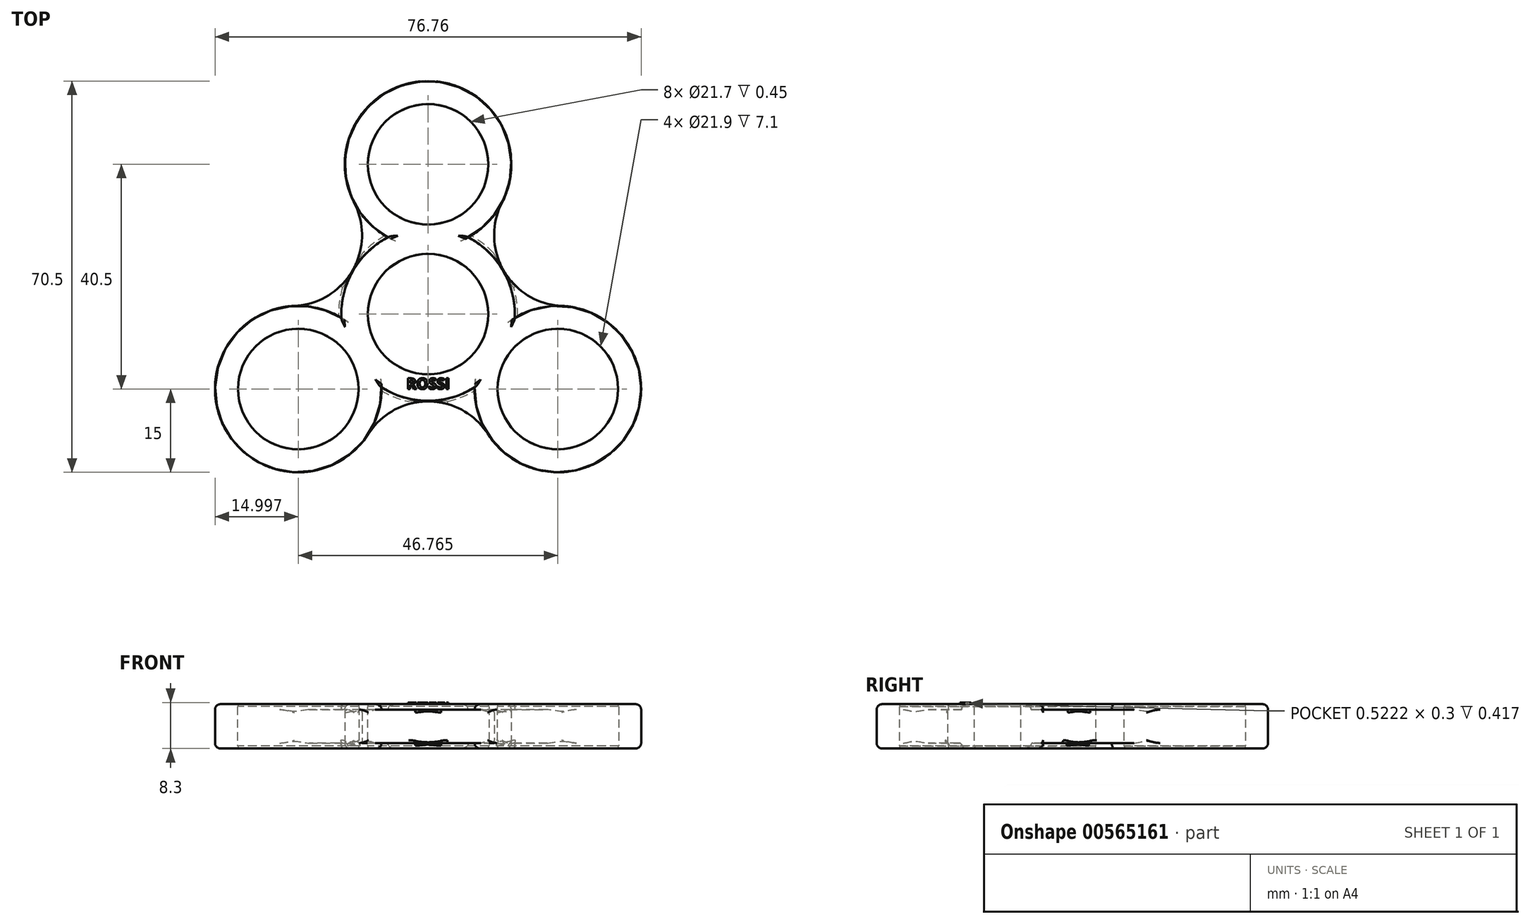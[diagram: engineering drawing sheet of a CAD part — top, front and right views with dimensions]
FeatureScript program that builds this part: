
annotation { "Feature Type Name" : "Feature", "Feature Type Description" : "" }
export const myFeature = defineFeature(function(context is Context, id is Id, definition is map)
    precondition{}
    {
        {
            var Q0;
            Q0=qCreatedBy(makeId("Top.planeOp"),FACE);
            var sketch = newSketch(context, id + "F0", { "sketchPlane" : qUnion([Q0])});
            skCircle(sketch, "E0", {"center": v(0, 0) * mm, "radius": 10.85 * mm});
            skCircle(sketch, "E1", {"center": v(0, 27) * mm, "radius": 10.85 * mm});
            skCircle(sketch, "E2.1.0", {"center": v(-23.38, -13.5) * mm, "radius": 10.85 * mm});
            skCircle(sketch, "E2.2.0", {"center": v(23.38, -13.5) * mm, "radius": 10.85 * mm});
            skArc(sketch, "E3", {"start": v(7.22, 13.85) * mm, "mid": v(0, 42) * mm, "end": v(-7.22, 13.85) * mm});
            skArc(sketch, "E4.1.0", {"start": v(8.39, -13.18) * mm, "mid": v(36.37, -21) * mm, "end": v(15.61, -0.67) * mm});
            skArc(sketch, "E4.2.0", {"start": v(-15.61, -0.67) * mm, "mid": v(-36.37, -21) * mm, "end": v(-8.39, -13.18) * mm});
            skArc(sketch, "E5", {"start": v(-8.39, -13.18) * mm, "mid": v(0, -15.62) * mm, "end": v(8.39, -13.18) * mm});
            skArc(sketch, "E6", {"start": v(-24.08, 1.48) * mm, "mid": v(-13.61, 7.86) * mm, "end": v(-13.33, 20.12) * mm});
            skArc(sketch, "E7", {"start": v(10.76, -21.6) * mm, "mid": v(0, -15.72) * mm, "end": v(-10.76, -21.6) * mm});
            skArc(sketch, "E8", {"start": v(13.33, 20.12) * mm, "mid": v(13.61, 7.86) * mm, "end": v(24.08, 1.48) * mm});
            skPoint(sketch, "E9.orphan", {"position": v(-13, 34.5) * mm});
            skPoint(sketch, "E10.orphan", {"position": v(-36.37, -6) * mm});
            skPoint(sketch, "E11.orphan", {"position": v(13, 34.5) * mm});
            skPoint(sketch, "E12.2.0.start.orphan", {"position": v(36.37, -6) * mm});
            skPoint(sketch, "E13.orphan", {"position": v(23.38, -28.5) * mm});
            skPoint(sketch, "E12.1.0.start.orphan", {"position": v(-23.38, -28.5) * mm});
            skArc(sketch, "E14.trimOffspring", {"start": v(15.61, -0.67) * mm, "mid": v(13.53, 7.81) * mm, "end": v(7.22, 13.85) * mm});
            skArc(sketch, "E15.trimOffspring", {"start": v(-7.22, 13.85) * mm, "mid": v(-13.53, 7.81) * mm, "end": v(-15.61, -0.67) * mm});
            skCircle(sketch, "E16", {"center": v(23.38, -13.5) * mm, "radius": 10.95 * mm});
            skCircle(sketch, "E17", {"center": v(-23.38, -13.5) * mm, "radius": 10.95 * mm});
            skCircle(sketch, "E18", {"center": v(0, 0) * mm, "radius": 10.95 * mm});
            skCircle(sketch, "E19", {"center": v(0, 27) * mm, "radius": 10.95 * mm});
            skSolve(sketch);
        }
        {
            var Q0;
            Q0=makeQuery(id+"F0.imprint","IMPRINT",FACE,{"disambiguationData":[TD([[makeQuery(id+"F0.imprint","IMPRINT",EDGE,{"derivedFrom":sQuery(id+"F0.wireOp",EDGE,"E2.1.0")}),-1.0]])]});
            var Q1;
            Q1=makeQuery(id+"F0.imprint","IMPRINT",FACE,{"disambiguationData":[TD([[makeQuery(id+"F0.imprint","IMPRINT",EDGE,{"derivedFrom":sQuery(id+"F0.wireOp",EDGE,"E0")}),-1.0]])]});
            var Q2;
            Q2=makeQuery(id+"F0.imprint","IMPRINT",FACE,{"disambiguationData":[TD([[makeQuery(id+"F0.imprint","IMPRINT",EDGE,{"derivedFrom":sQuery(id+"F0.wireOp",EDGE,"E1")}),-1.0]])]});
            var Q3;
            {var subQ0=sQuery(id+"F0.wireOp",EDGE,"E3");var subQ1=sQuery(id+"F0.wireOp",EDGE,"KJlQqC9l-gusD-toYh-YzLE-zyJcLNbmcpUm");var subQ2=makeQuery(id+"F0.imprint","INTERSECT",VERTEX,{"derivedFrom":[subQ1,subQ0]});Q3=makeQuery(id+"F0.imprint","IMPRINT",FACE,{"disambiguationData":[TD([[makeQuery(id+"F0.imprint","IMPRINT",EDGE,{"disambiguationData":[TD([[subQ2,1.0]])],"derivedFrom":subQ1}),1.0]])]});}
            var Q4;
            {var subQ0=sQuery(id+"F0.wireOp",EDGE,"E3");var subQ1=sQuery(id+"F0.wireOp",EDGE,"KJlQqC9l-gusD-toYh-YzLE-zyJcLNbmcpUm");var subQ2=makeQuery(id+"F0.imprint","INTERSECT",VERTEX,{"derivedFrom":[subQ1,subQ0]});Q4=makeQuery(id+"F0.imprint","IMPRINT",FACE,{"disambiguationData":[TD([[makeQuery(id+"F0.imprint","IMPRINT",EDGE,{"disambiguationData":[TD([[subQ2,1.0]])],"derivedFrom":subQ1}),-1.0]])]});}
            var Q5;
            {var subQ0=sQuery(id+"F0.wireOp",EDGE,"E5");var subQ1=sQuery(id+"F0.wireOp",EDGE,"E4.2.0");var subQ2=makeQuery(id+"F0.imprint","INTERSECT",VERTEX,{"disambiguationData":[OD(0.0)],"derivedFrom":[subQ1,subQ0]});Q5=makeQuery(id+"F0.imprint","IMPRINT",FACE,{"disambiguationData":[TD([[makeQuery(id+"F0.imprint","IMPRINT",EDGE,{"disambiguationData":[TD([[subQ2,-1.0]])],"derivedFrom":subQ1}),1.0]])]});}
            var Q6;
            Q6=makeQuery(id+"F0.imprint","IMPRINT",FACE,{"disambiguationData":[TD([[makeQuery(id+"F0.imprint","IMPRINT",EDGE,{"derivedFrom":sQuery(id+"F0.wireOp",EDGE,"E2.2.0")}),-1.0]])]});
            var Q7;
            {var subQ0=sQuery(id+"F0.wireOp",EDGE,"E5");var subQ1=sQuery(id+"F0.wireOp",EDGE,"E4.1.0");var subQ2=makeQuery(id+"F0.imprint","INTERSECT",VERTEX,{"disambiguationData":[OD(0.0)],"derivedFrom":[subQ1,subQ0]});Q7=makeQuery(id+"F0.imprint","IMPRINT",FACE,{"disambiguationData":[TD([[makeQuery(id+"F0.imprint","IMPRINT",EDGE,{"disambiguationData":[TD([[subQ2,-1.0]])],"derivedFrom":subQ1}),1.0]])]});}
            extrude(context, id + "F1", {"entities" : qUnion([Q0, Q1, Q2, Q3, Q4, Q5, Q6, Q7]), "endBound" : BoundingType.SYMMETRIC, "depth" : 8 * mm, "offsetDistance" : 25 * mm});
        }
        {
            var Q0;
            {var subQ0=sQuery(id+"F0.wireOp",EDGE,"E7");Q0=makeQuery(id+"F0.imprint","IMPRINT",FACE,{"disambiguationData":[TD([[makeQuery(id+"F0.imprint","IMPRINT",EDGE,{"derivedFrom":subQ0}),-1.0]])]});}
            var Q1;
            {var subQ0=sQuery(id+"F0.wireOp",EDGE,"E6");Q1=makeQuery(id+"F0.imprint","IMPRINT",FACE,{"disambiguationData":[TD([[makeQuery(id+"F0.imprint","IMPRINT",EDGE,{"derivedFrom":subQ0}),-1.0]])]});}
            var Q2;
            {var subQ0=sQuery(id+"F0.wireOp",EDGE,"E8");Q2=makeQuery(id+"F0.imprint","IMPRINT",FACE,{"disambiguationData":[TD([[makeQuery(id+"F0.imprint","IMPRINT",EDGE,{"derivedFrom":subQ0}),-1.0]])]});}
            extrude(context, id + "F2", {"entities" : qUnion([Q0, Q1, Q2]), "operationType" : NewBodyOperationType.ADD, "endBound" : BoundingType.SYMMETRIC, "depth" : 6 * mm, "offsetDistance" : 25 * mm});
        }
        {
            var Q0;
            Q0=makeQuery(id+"F1.opExtrude","CAP_EDGE",EDGE,{"disambiguationData":[OSD([sQuery(id+"F0.wireOp",EDGE,"E15.trimOffspring")])],"isStart":true});
            var Q1;
            Q1=makeQuery(id+"F2.opExtrude","CAP_EDGE",EDGE,{"disambiguationData":[OSD([sQuery(id+"F0.wireOp",EDGE,"E15.trimOffspring")])],"isStart":true});
            var Q2;
            Q2=makeQuery(id+"F1.opExtrude","CAP_EDGE",EDGE,{"disambiguationData":[OSD([sQuery(id+"F0.wireOp",EDGE,"E5")])],"isStart":true});
            var Q3;
            Q3=makeQuery(id+"F2.opExtrude","CAP_EDGE",EDGE,{"disambiguationData":[OSD([sQuery(id+"F0.wireOp",EDGE,"E5")])],"isStart":true});
            var Q4;
            Q4=makeQuery(id+"F1.opExtrude","CAP_EDGE",EDGE,{"disambiguationData":[OSD([sQuery(id+"F0.wireOp",EDGE,"E14.trimOffspring")])],"isStart":true});
            var Q5;
            Q5=makeQuery(id+"F2.opExtrude","CAP_EDGE",EDGE,{"disambiguationData":[OSD([sQuery(id+"F0.wireOp",EDGE,"E14.trimOffspring")])],"isStart":true});
            fillet(context, id + "F3", {"entities" : qUnion([Q0, Q1, Q2, Q3, Q4, Q5]), "radius" : 0.5 * mm, "rho" : 0.5, "crossSection" : FilletCrossSection.CONIC, "allowEdgeOverflow" : false});
        }
        {
            var Q0;
            Q0=makeQuery(id+"F1.opExtrude","CAP_EDGE",EDGE,{"disambiguationData":[OSD([sQuery(id+"F0.wireOp",EDGE,"E5")])],"isStart":false});
            var Q1;
            Q1=makeQuery(id+"F2.opExtrude","CAP_EDGE",EDGE,{"disambiguationData":[OSD([sQuery(id+"F0.wireOp",EDGE,"E5")])],"isStart":false});
            var Q2;
            Q2=makeQuery(id+"F1.opExtrude","CAP_EDGE",EDGE,{"disambiguationData":[OSD([sQuery(id+"F0.wireOp",EDGE,"E14.trimOffspring")])],"isStart":false});
            var Q3;
            Q3=makeQuery(id+"F2.opExtrude","CAP_EDGE",EDGE,{"disambiguationData":[OSD([sQuery(id+"F0.wireOp",EDGE,"E14.trimOffspring")])],"isStart":false});
            var Q4;
            Q4=makeQuery(id+"F1.opExtrude","CAP_EDGE",EDGE,{"disambiguationData":[OSD([sQuery(id+"F0.wireOp",EDGE,"E15.trimOffspring")])],"isStart":false});
            var Q5;
            Q5=makeQuery(id+"F2.opExtrude","CAP_EDGE",EDGE,{"disambiguationData":[OSD([sQuery(id+"F0.wireOp",EDGE,"E15.trimOffspring")])],"isStart":false});
            fillet(context, id + "F4", {"entities" : qUnion([Q0, Q1, Q2, Q3, Q4, Q5]), "radius" : 0.5 * mm, "rho" : 0.5, "crossSection" : FilletCrossSection.CONIC, "allowEdgeOverflow" : false});
        }
        {
            var Q0;
            Q0=makeQuery(id+"F1.opExtrude","CAP_EDGE",EDGE,{"disambiguationData":[OSD([sQuery(id+"F0.wireOp",EDGE,"E4.1.0")])],"isStart":false});
            var Q1;
            Q1=makeQuery(id+"F1.opExtrude","CAP_EDGE",EDGE,{"disambiguationData":[OSD([sQuery(id+"F0.wireOp",EDGE,"E3")])],"isStart":false});
            var Q2;
            Q2=makeQuery(id+"F1.opExtrude","CAP_EDGE",EDGE,{"disambiguationData":[OSD([sQuery(id+"F0.wireOp",EDGE,"E4.2.0")])],"isStart":false});
            var Q3;
            Q3=makeQuery(id+"F1.opExtrude","CAP_EDGE",EDGE,{"disambiguationData":[OSD([sQuery(id+"F0.wireOp",EDGE,"E4.2.0")])],"isStart":true});
            var Q4;
            Q4=makeQuery(id+"F1.opExtrude","CAP_EDGE",EDGE,{"disambiguationData":[OSD([sQuery(id+"F0.wireOp",EDGE,"E4.1.0")])],"isStart":true});
            var Q5;
            Q5=makeQuery(id+"F1.opExtrude","CAP_EDGE",EDGE,{"disambiguationData":[OSD([sQuery(id+"F0.wireOp",EDGE,"E3")])],"isStart":true});
            fillet(context, id + "F5", {"entities" : qUnion([Q0, Q1, Q2, Q3, Q4, Q5]), "radius" : 1 * mm, "allowEdgeOverflow" : false});
        }
        {
            var Q0;
            Q0=makeQuery(id+"F2.opExtrude","SWEPT_FACE",FACE,{"disambiguationData":[OSD([sQuery(id+"F0.wireOp",EDGE,"E8")])]});
            var Q1;
            Q1=makeQuery(id+"F2.opExtrude","SWEPT_FACE",FACE,{"disambiguationData":[OSD([sQuery(id+"F0.wireOp",EDGE,"E6")])]});
            var Q2;
            Q2=makeQuery(id+"F2.opExtrude","SWEPT_FACE",FACE,{"disambiguationData":[OSD([sQuery(id+"F0.wireOp",EDGE,"E7")])]});
            fillet(context, id + "F6", {"entities" : qUnion([Q0, Q1, Q2]), "radius" : .5 * mm, "tangentPropagation" : true, "allowEdgeOverflow" : false});
        }
        {
            var Q0;
            Q0=makeQuery(id+"F0.imprint","IMPRINT",FACE,{"disambiguationData":[TD([[makeQuery(id+"F0.imprint","IMPRINT",EDGE,{"derivedFrom":sQuery(id+"F0.wireOp",EDGE,"E19")}),1.0]])]});
            var Q1;
            Q1=makeQuery(id+"F0.imprint","IMPRINT",FACE,{"disambiguationData":[TD([[makeQuery(id+"F0.imprint","IMPRINT",EDGE,{"derivedFrom":sQuery(id+"F0.wireOp",EDGE,"E18")}),1.0]])]});
            var Q2;
            Q2=makeQuery(id+"F0.imprint","IMPRINT",FACE,{"disambiguationData":[TD([[makeQuery(id+"F0.imprint","IMPRINT",EDGE,{"derivedFrom":sQuery(id+"F0.wireOp",EDGE,"E16")}),1.0]])]});
            var Q3;
            Q3=makeQuery(id+"F0.imprint","IMPRINT",FACE,{"disambiguationData":[TD([[makeQuery(id+"F0.imprint","IMPRINT",EDGE,{"derivedFrom":sQuery(id+"F0.wireOp",EDGE,"E17")}),1.0]])]});
            extrude(context, id + "F7", {"entities" : qUnion([Q0, Q1, Q2, Q3]), "endBound" : BoundingType.SYMMETRIC, "depth" : 7.1 * mm, "offsetDistance" : 25 * mm});
        }
        {
            var Q0;
            Q0=makeQuery(id+"F7.opExtrude","SWEPT_BODY",BODY,{"disambiguationData":[OSD([sQuery(id+"F0.wireOp",EDGE,"E16")])]});
            var Q1;
            Q1=makeQuery(id+"F7.opExtrude","SWEPT_BODY",BODY,{"disambiguationData":[OSD([sQuery(id+"F0.wireOp",EDGE,"E17")])]});
            var Q2;
            Q2=makeQuery(id+"F7.opExtrude","SWEPT_BODY",BODY,{"disambiguationData":[OSD([sQuery(id+"F0.wireOp",EDGE,"E18")])]});
            var Q3;
            Q3=makeQuery(id+"F7.opExtrude","SWEPT_BODY",BODY,{"disambiguationData":[OSD([sQuery(id+"F0.wireOp",EDGE,"E19")])]});
            var Q4;
            Q4=makeQuery(id+"F1.opExtrude","SWEPT_BODY",BODY,{"disambiguationData":[OSD([sQuery(id+"F0.wireOp",EDGE,"E0"),sQuery(id+"F0.wireOp",EDGE,"E1"),sQuery(id+"F0.wireOp",EDGE,"E2.1.0"),sQuery(id+"F0.wireOp",EDGE,"E2.2.0"),sQuery(id+"F0.wireOp",EDGE,"E3"),sQuery(id+"F0.wireOp",EDGE,"E4.1.0"),sQuery(id+"F0.wireOp",EDGE,"E4.2.0"),sQuery(id+"F0.wireOp",EDGE,"E5"),sQuery(id+"F0.wireOp",EDGE,"E14.trimOffspring"),sQuery(id+"F0.wireOp",EDGE,"E15.trimOffspring"),sQuery(id+"F0.wireOp",EDGE,"f471b002-4030-4226-8843-a168e7eb6244.sketch_text.stroke-7"),sQuery(id+"F0.wireOp",EDGE,"f471b002-4030-4226-8843-a168e7eb6244.sketch_text.stroke-8"),sQuery(id+"F0.wireOp",EDGE,"f471b002-4030-4226-8843-a168e7eb6244.sketch_text.stroke-9"),sQuery(id+"F0.wireOp",EDGE,"f471b002-4030-4226-8843-a168e7eb6244.sketch_text.stroke-10"),sQuery(id+"F0.wireOp",EDGE,"f471b002-4030-4226-8843-a168e7eb6244.sketch_text.stroke-11"),sQuery(id+"F0.wireOp",EDGE,"f471b002-4030-4226-8843-a168e7eb6244.sketch_text.stroke-12"),sQuery(id+"F0.wireOp",EDGE,"f471b002-4030-4226-8843-a168e7eb6244.sketch_text.stroke-13"),sQuery(id+"F0.wireOp",EDGE,"f471b002-4030-4226-8843-a168e7eb6244.sketch_text.stroke-14"),sQuery(id+"F0.wireOp",EDGE,"f471b002-4030-4226-8843-a168e7eb6244.sketch_text.stroke-15"),sQuery(id+"F0.wireOp",EDGE,"f471b002-4030-4226-8843-a168e7eb6244.sketch_text.stroke-16"),sQuery(id+"F0.wireOp",EDGE,"f471b002-4030-4226-8843-a168e7eb6244.sketch_text.stroke-17"),sQuery(id+"F0.wireOp",EDGE,"f471b002-4030-4226-8843-a168e7eb6244.sketch_text.stroke-18"),sQuery(id+"F0.wireOp",EDGE,"f471b002-4030-4226-8843-a168e7eb6244.sketch_text.stroke-19"),sQuery(id+"F0.wireOp",EDGE,"f471b002-4030-4226-8843-a168e7eb6244.sketch_text.stroke-20"),sQuery(id+"F0.wireOp",EDGE,"f471b002-4030-4226-8843-a168e7eb6244.sketch_text.stroke-21"),sQuery(id+"F0.wireOp",EDGE,"f471b002-4030-4226-8843-a168e7eb6244.sketch_text.stroke-22"),sQuery(id+"F0.wireOp",EDGE,"f471b002-4030-4226-8843-a168e7eb6244.sketch_text.stroke-23"),sQuery(id+"F0.wireOp",EDGE,"f471b002-4030-4226-8843-a168e7eb6244.sketch_text.stroke-28"),sQuery(id+"F0.wireOp",EDGE,"f471b002-4030-4226-8843-a168e7eb6244.sketch_text.stroke-29"),sQuery(id+"F0.wireOp",EDGE,"f471b002-4030-4226-8843-a168e7eb6244.sketch_text.stroke-30"),sQuery(id+"F0.wireOp",EDGE,"f471b002-4030-4226-8843-a168e7eb6244.sketch_text.stroke-31"),sQuery(id+"F0.wireOp",EDGE,"f471b002-4030-4226-8843-a168e7eb6244.sketch_text.stroke-32"),sQuery(id+"F0.wireOp",EDGE,"f471b002-4030-4226-8843-a168e7eb6244.sketch_text.stroke-33"),sQuery(id+"F0.wireOp",EDGE,"f471b002-4030-4226-8843-a168e7eb6244.sketch_text.stroke-34"),sQuery(id+"F0.wireOp",EDGE,"f471b002-4030-4226-8843-a168e7eb6244.sketch_text.stroke-35"),sQuery(id+"F0.wireOp",EDGE,"f471b002-4030-4226-8843-a168e7eb6244.sketch_text.stroke-36"),sQuery(id+"F0.wireOp",EDGE,"f471b002-4030-4226-8843-a168e7eb6244.sketch_text.stroke-37"),sQuery(id+"F0.wireOp",EDGE,"f471b002-4030-4226-8843-a168e7eb6244.sketch_text.stroke-38"),sQuery(id+"F0.wireOp",EDGE,"f471b002-4030-4226-8843-a168e7eb6244.sketch_text.stroke-39"),sQuery(id+"F0.wireOp",EDGE,"f471b002-4030-4226-8843-a168e7eb6244.sketch_text.stroke-40"),sQuery(id+"F0.wireOp",EDGE,"f471b002-4030-4226-8843-a168e7eb6244.sketch_text.stroke-41"),sQuery(id+"F0.wireOp",EDGE,"f471b002-4030-4226-8843-a168e7eb6244.sketch_text.stroke-42"),sQuery(id+"F0.wireOp",EDGE,"f471b002-4030-4226-8843-a168e7eb6244.sketch_text.stroke-43"),sQuery(id+"F0.wireOp",EDGE,"f471b002-4030-4226-8843-a168e7eb6244.sketch_text.stroke-44"),sQuery(id+"F0.wireOp",EDGE,"f471b002-4030-4226-8843-a168e7eb6244.sketch_text.stroke-45"),sQuery(id+"F0.wireOp",EDGE,"f471b002-4030-4226-8843-a168e7eb6244.sketch_text.stroke-46"),sQuery(id+"F0.wireOp",EDGE,"f471b002-4030-4226-8843-a168e7eb6244.sketch_text.stroke-47"),sQuery(id+"F0.wireOp",EDGE,"f471b002-4030-4226-8843-a168e7eb6244.sketch_text.stroke-48"),sQuery(id+"F0.wireOp",EDGE,"f471b002-4030-4226-8843-a168e7eb6244.sketch_text.stroke-49"),sQuery(id+"F0.wireOp",EDGE,"f471b002-4030-4226-8843-a168e7eb6244.sketch_text.stroke-50"),sQuery(id+"F0.wireOp",EDGE,"f471b002-4030-4226-8843-a168e7eb6244.sketch_text.stroke-51"),sQuery(id+"F0.wireOp",EDGE,"f471b002-4030-4226-8843-a168e7eb6244.sketch_text.stroke-52"),sQuery(id+"F0.wireOp",EDGE,"f471b002-4030-4226-8843-a168e7eb6244.sketch_text.stroke-53"),sQuery(id+"F0.wireOp",EDGE,"f471b002-4030-4226-8843-a168e7eb6244.sketch_text.stroke-54"),sQuery(id+"F0.wireOp",EDGE,"f471b002-4030-4226-8843-a168e7eb6244.sketch_text.stroke-55"),sQuery(id+"F0.wireOp",EDGE,"f471b002-4030-4226-8843-a168e7eb6244.sketch_text.stroke-56"),sQuery(id+"F0.wireOp",EDGE,"f471b002-4030-4226-8843-a168e7eb6244.sketch_text.stroke-57"),sQuery(id+"F0.wireOp",EDGE,"f471b002-4030-4226-8843-a168e7eb6244.sketch_text.stroke-58"),sQuery(id+"F0.wireOp",EDGE,"f471b002-4030-4226-8843-a168e7eb6244.sketch_text.stroke-59"),sQuery(id+"F0.wireOp",EDGE,"f471b002-4030-4226-8843-a168e7eb6244.sketch_text.stroke-60"),sQuery(id+"F0.wireOp",EDGE,"f471b002-4030-4226-8843-a168e7eb6244.sketch_text.stroke-74"),sQuery(id+"F0.wireOp",EDGE,"f471b002-4030-4226-8843-a168e7eb6244.sketch_text.stroke-75"),sQuery(id+"F0.wireOp",EDGE,"f471b002-4030-4226-8843-a168e7eb6244.sketch_text.stroke-76"),sQuery(id+"F0.wireOp",EDGE,"f471b002-4030-4226-8843-a168e7eb6244.sketch_text.stroke-77"),sQuery(id+"F0.wireOp",EDGE,"f471b002-4030-4226-8843-a168e7eb6244.sketch_text.stroke-78"),sQuery(id+"F0.wireOp",EDGE,"f471b002-4030-4226-8843-a168e7eb6244.sketch_text.stroke-79"),sQuery(id+"F0.wireOp",EDGE,"f471b002-4030-4226-8843-a168e7eb6244.sketch_text.stroke-80"),sQuery(id+"F0.wireOp",EDGE,"f471b002-4030-4226-8843-a168e7eb6244.sketch_text.stroke-81"),sQuery(id+"F0.wireOp",EDGE,"f471b002-4030-4226-8843-a168e7eb6244.sketch_text.stroke-86"),sQuery(id+"F0.wireOp",EDGE,"f471b002-4030-4226-8843-a168e7eb6244.sketch_text.stroke-87"),sQuery(id+"F0.wireOp",EDGE,"f471b002-4030-4226-8843-a168e7eb6244.sketch_text.stroke-88"),sQuery(id+"F0.wireOp",EDGE,"f471b002-4030-4226-8843-a168e7eb6244.sketch_text.stroke-89"),sQuery(id+"F0.wireOp",EDGE,"f471b002-4030-4226-8843-a168e7eb6244.sketch_text.stroke-90"),sQuery(id+"F0.wireOp",EDGE,"f471b002-4030-4226-8843-a168e7eb6244.sketch_text.stroke-91"),sQuery(id+"F0.wireOp",EDGE,"f471b002-4030-4226-8843-a168e7eb6244.sketch_text.stroke-92"),sQuery(id+"F0.wireOp",EDGE,"f471b002-4030-4226-8843-a168e7eb6244.sketch_text.stroke-93"),sQuery(id+"F0.wireOp",EDGE,"f471b002-4030-4226-8843-a168e7eb6244.sketch_text.stroke-94"),sQuery(id+"F0.wireOp",EDGE,"f471b002-4030-4226-8843-a168e7eb6244.sketch_text.stroke-95"),sQuery(id+"F0.wireOp",EDGE,"f471b002-4030-4226-8843-a168e7eb6244.sketch_text.stroke-96"),sQuery(id+"F0.wireOp",EDGE,"f471b002-4030-4226-8843-a168e7eb6244.sketch_text.stroke-97"),sQuery(id+"F0.wireOp",EDGE,"f471b002-4030-4226-8843-a168e7eb6244.sketch_text.stroke-98"),sQuery(id+"F0.wireOp",EDGE,"f471b002-4030-4226-8843-a168e7eb6244.sketch_text.stroke-99"),sQuery(id+"F0.wireOp",EDGE,"f471b002-4030-4226-8843-a168e7eb6244.sketch_text.stroke-100"),sQuery(id+"F0.wireOp",EDGE,"f471b002-4030-4226-8843-a168e7eb6244.sketch_text.stroke-101"),sQuery(id+"F0.wireOp",EDGE,"f471b002-4030-4226-8843-a168e7eb6244.sketch_text.stroke-102"),sQuery(id+"F0.wireOp",EDGE,"f471b002-4030-4226-8843-a168e7eb6244.sketch_text.stroke-103"),sQuery(id+"F0.wireOp",EDGE,"f471b002-4030-4226-8843-a168e7eb6244.sketch_text.stroke-104"),sQuery(id+"F0.wireOp",EDGE,"f471b002-4030-4226-8843-a168e7eb6244.sketch_text.stroke-105"),sQuery(id+"F0.wireOp",EDGE,"f471b002-4030-4226-8843-a168e7eb6244.sketch_text.stroke-106"),sQuery(id+"F0.wireOp",EDGE,"f471b002-4030-4226-8843-a168e7eb6244.sketch_text.stroke-107"),sQuery(id+"F0.wireOp",EDGE,"f471b002-4030-4226-8843-a168e7eb6244.sketch_text.stroke-108"),sQuery(id+"F0.wireOp",EDGE,"f471b002-4030-4226-8843-a168e7eb6244.sketch_text.stroke-109"),sQuery(id+"F0.wireOp",EDGE,"f471b002-4030-4226-8843-a168e7eb6244.sketch_text.stroke-110"),sQuery(id+"F0.wireOp",EDGE,"f471b002-4030-4226-8843-a168e7eb6244.sketch_text.stroke-111"),sQuery(id+"F0.wireOp",EDGE,"f471b002-4030-4226-8843-a168e7eb6244.sketch_text.stroke-112"),sQuery(id+"F0.wireOp",EDGE,"f471b002-4030-4226-8843-a168e7eb6244.sketch_text.stroke-113"),sQuery(id+"F0.wireOp",EDGE,"f471b002-4030-4226-8843-a168e7eb6244.sketch_text.stroke-114"),sQuery(id+"F0.wireOp",EDGE,"f471b002-4030-4226-8843-a168e7eb6244.sketch_text.stroke-115"),sQuery(id+"F0.wireOp",EDGE,"f471b002-4030-4226-8843-a168e7eb6244.sketch_text.stroke-116"),sQuery(id+"F0.wireOp",EDGE,"f471b002-4030-4226-8843-a168e7eb6244.sketch_text.stroke-117"),sQuery(id+"F0.wireOp",EDGE,"f471b002-4030-4226-8843-a168e7eb6244.sketch_text.stroke-118"),sQuery(id+"F0.wireOp",EDGE,"f471b002-4030-4226-8843-a168e7eb6244.sketch_text.stroke-119"),sQuery(id+"F0.wireOp",EDGE,"f471b002-4030-4226-8843-a168e7eb6244.sketch_text.stroke-120"),sQuery(id+"F0.wireOp",EDGE,"f471b002-4030-4226-8843-a168e7eb6244.sketch_text.stroke-121"),sQuery(id+"F0.wireOp",EDGE,"f471b002-4030-4226-8843-a168e7eb6244.sketch_text.stroke-122"),sQuery(id+"F0.wireOp",EDGE,"f471b002-4030-4226-8843-a168e7eb6244.sketch_text.stroke-123"),sQuery(id+"F0.wireOp",EDGE,"f471b002-4030-4226-8843-a168e7eb6244.sketch_text.stroke-124"),sQuery(id+"F0.wireOp",EDGE,"f471b002-4030-4226-8843-a168e7eb6244.sketch_text.stroke-125"),sQuery(id+"F0.wireOp",EDGE,"f471b002-4030-4226-8843-a168e7eb6244.sketch_text.stroke-126"),sQuery(id+"F0.wireOp",EDGE,"f471b002-4030-4226-8843-a168e7eb6244.sketch_text.stroke-127"),sQuery(id+"F0.wireOp",EDGE,"f471b002-4030-4226-8843-a168e7eb6244.sketch_text.stroke-128"),sQuery(id+"F0.wireOp",EDGE,"f471b002-4030-4226-8843-a168e7eb6244.sketch_text.stroke-129"),sQuery(id+"F0.wireOp",EDGE,"f471b002-4030-4226-8843-a168e7eb6244.sketch_text.stroke-130"),sQuery(id+"F0.wireOp",EDGE,"f471b002-4030-4226-8843-a168e7eb6244.sketch_text.stroke-131"),sQuery(id+"F0.wireOp",EDGE,"f471b002-4030-4226-8843-a168e7eb6244.sketch_text.stroke-132"),sQuery(id+"F0.wireOp",EDGE,"f471b002-4030-4226-8843-a168e7eb6244.sketch_text.stroke-133"),sQuery(id+"F0.wireOp",EDGE,"f471b002-4030-4226-8843-a168e7eb6244.sketch_text.stroke-134"),sQuery(id+"F0.wireOp",EDGE,"f471b002-4030-4226-8843-a168e7eb6244.sketch_text.stroke-135"),sQuery(id+"F0.wireOp",EDGE,"f471b002-4030-4226-8843-a168e7eb6244.sketch_text.stroke-136"),sQuery(id+"F0.wireOp",EDGE,"f471b002-4030-4226-8843-a168e7eb6244.sketch_text.stroke-137"),sQuery(id+"F0.wireOp",EDGE,"f471b002-4030-4226-8843-a168e7eb6244.sketch_text.stroke-138"),sQuery(id+"F0.wireOp",EDGE,"f471b002-4030-4226-8843-a168e7eb6244.sketch_text.stroke-139"),sQuery(id+"F0.wireOp",EDGE,"f471b002-4030-4226-8843-a168e7eb6244.sketch_text.stroke-140"),sQuery(id+"F0.wireOp",EDGE,"f471b002-4030-4226-8843-a168e7eb6244.sketch_text.stroke-141"),sQuery(id+"F0.wireOp",EDGE,"f471b002-4030-4226-8843-a168e7eb6244.sketch_text.stroke-142"),sQuery(id+"F0.wireOp",EDGE,"f471b002-4030-4226-8843-a168e7eb6244.sketch_text.stroke-143"),sQuery(id+"F0.wireOp",EDGE,"f471b002-4030-4226-8843-a168e7eb6244.sketch_text.stroke-144"),sQuery(id+"F0.wireOp",EDGE,"f471b002-4030-4226-8843-a168e7eb6244.sketch_text.stroke-145"),sQuery(id+"F0.wireOp",EDGE,"f471b002-4030-4226-8843-a168e7eb6244.sketch_text.stroke-146"),sQuery(id+"F0.wireOp",EDGE,"f471b002-4030-4226-8843-a168e7eb6244.sketch_text.stroke-147"),sQuery(id+"F0.wireOp",EDGE,"f471b002-4030-4226-8843-a168e7eb6244.sketch_text.stroke-148"),sQuery(id+"F0.wireOp",EDGE,"f471b002-4030-4226-8843-a168e7eb6244.sketch_text.stroke-149"),sQuery(id+"F0.wireOp",EDGE,"f471b002-4030-4226-8843-a168e7eb6244.sketch_text.stroke-150"),sQuery(id+"F0.wireOp",EDGE,"f471b002-4030-4226-8843-a168e7eb6244.sketch_text.stroke-151"),sQuery(id+"F0.wireOp",EDGE,"f471b002-4030-4226-8843-a168e7eb6244.sketch_text.stroke-152"),sQuery(id+"F0.wireOp",EDGE,"f471b002-4030-4226-8843-a168e7eb6244.sketch_text.stroke-153"),sQuery(id+"F0.wireOp",EDGE,"f471b002-4030-4226-8843-a168e7eb6244.sketch_text.stroke-154"),sQuery(id+"F0.wireOp",EDGE,"f471b002-4030-4226-8843-a168e7eb6244.sketch_text.stroke-155"),sQuery(id+"F0.wireOp",EDGE,"f471b002-4030-4226-8843-a168e7eb6244.sketch_text.stroke-156"),sQuery(id+"F0.wireOp",EDGE,"f471b002-4030-4226-8843-a168e7eb6244.sketch_text.stroke-157"),sQuery(id+"F0.wireOp",EDGE,"f471b002-4030-4226-8843-a168e7eb6244.sketch_text.stroke-158"),sQuery(id+"F0.wireOp",EDGE,"f471b002-4030-4226-8843-a168e7eb6244.sketch_text.stroke-159"),sQuery(id+"F0.wireOp",EDGE,"f471b002-4030-4226-8843-a168e7eb6244.sketch_text.stroke-160"),sQuery(id+"F0.wireOp",EDGE,"f471b002-4030-4226-8843-a168e7eb6244.sketch_text.stroke-161"),sQuery(id+"F0.wireOp",EDGE,"f471b002-4030-4226-8843-a168e7eb6244.sketch_text.stroke-162"),sQuery(id+"F0.wireOp",EDGE,"f471b002-4030-4226-8843-a168e7eb6244.sketch_text.stroke-163"),sQuery(id+"F0.wireOp",EDGE,"f471b002-4030-4226-8843-a168e7eb6244.sketch_text.stroke-164"),sQuery(id+"F0.wireOp",EDGE,"f471b002-4030-4226-8843-a168e7eb6244.sketch_text.stroke-165"),sQuery(id+"F0.wireOp",EDGE,"f471b002-4030-4226-8843-a168e7eb6244.sketch_text.stroke-166"),sQuery(id+"F0.wireOp",EDGE,"f471b002-4030-4226-8843-a168e7eb6244.sketch_text.stroke-167"),sQuery(id+"F0.wireOp",EDGE,"f471b002-4030-4226-8843-a168e7eb6244.sketch_text.stroke-168"),sQuery(id+"F0.wireOp",EDGE,"f471b002-4030-4226-8843-a168e7eb6244.sketch_text.stroke-169"),sQuery(id+"F0.wireOp",EDGE,"f471b002-4030-4226-8843-a168e7eb6244.sketch_text.stroke-170")])]});
            booleanBodies(context, id + "F8", {"operationType" : BooleanOperationType.SUBTRACTION, "tools" : qUnion([Q0, Q1, Q2, Q3]), "targets" : qUnion([Q4])});
        }
        {
            var Q0;
            Q0=makeQuery(id+"F1.opExtrude","CAP_FACE",FACE,{"disambiguationData":[OSD([sQuery(id+"F0.wireOp",EDGE,"E0"),sQuery(id+"F0.wireOp",EDGE,"E1"),sQuery(id+"F0.wireOp",EDGE,"E2.1.0"),sQuery(id+"F0.wireOp",EDGE,"E2.2.0"),sQuery(id+"F0.wireOp",EDGE,"E3"),sQuery(id+"F0.wireOp",EDGE,"E4.1.0"),sQuery(id+"F0.wireOp",EDGE,"E4.2.0"),sQuery(id+"F0.wireOp",EDGE,"E5"),sQuery(id+"F0.wireOp",EDGE,"E14.trimOffspring"),sQuery(id+"F0.wireOp",EDGE,"E15.trimOffspring")])],"isStart":false});
            var sketch = newSketch(context, id + "F9", { "sketchPlane" : qUnion([Q0])});
            skText(sketch, "E20", { "text": "ROSSI", "fontName": "OpenSans-Bold.ttf"});
            skLineSegment(sketch, "E21", {"start": v(0, 0) * mm, "end": v(0, -20.78) * mm});
            const initialGuessF9  = {"E20": [-0.00388, -0.0135, 1, 0, 0.00195]};
            skSetInitialGuess(sketch, initialGuessF9);
            skSolve(sketch);
        }
        {
            var Q0;
            Q0=qSketchRegion(id+"F9",true);
            extrude(context, id + "F10", {"entities" : qUnion([Q0]), "operationType" : NewBodyOperationType.ADD, "depth" : 0.3 * mm, "offsetDistance" : 25 * mm});
        }
    });
